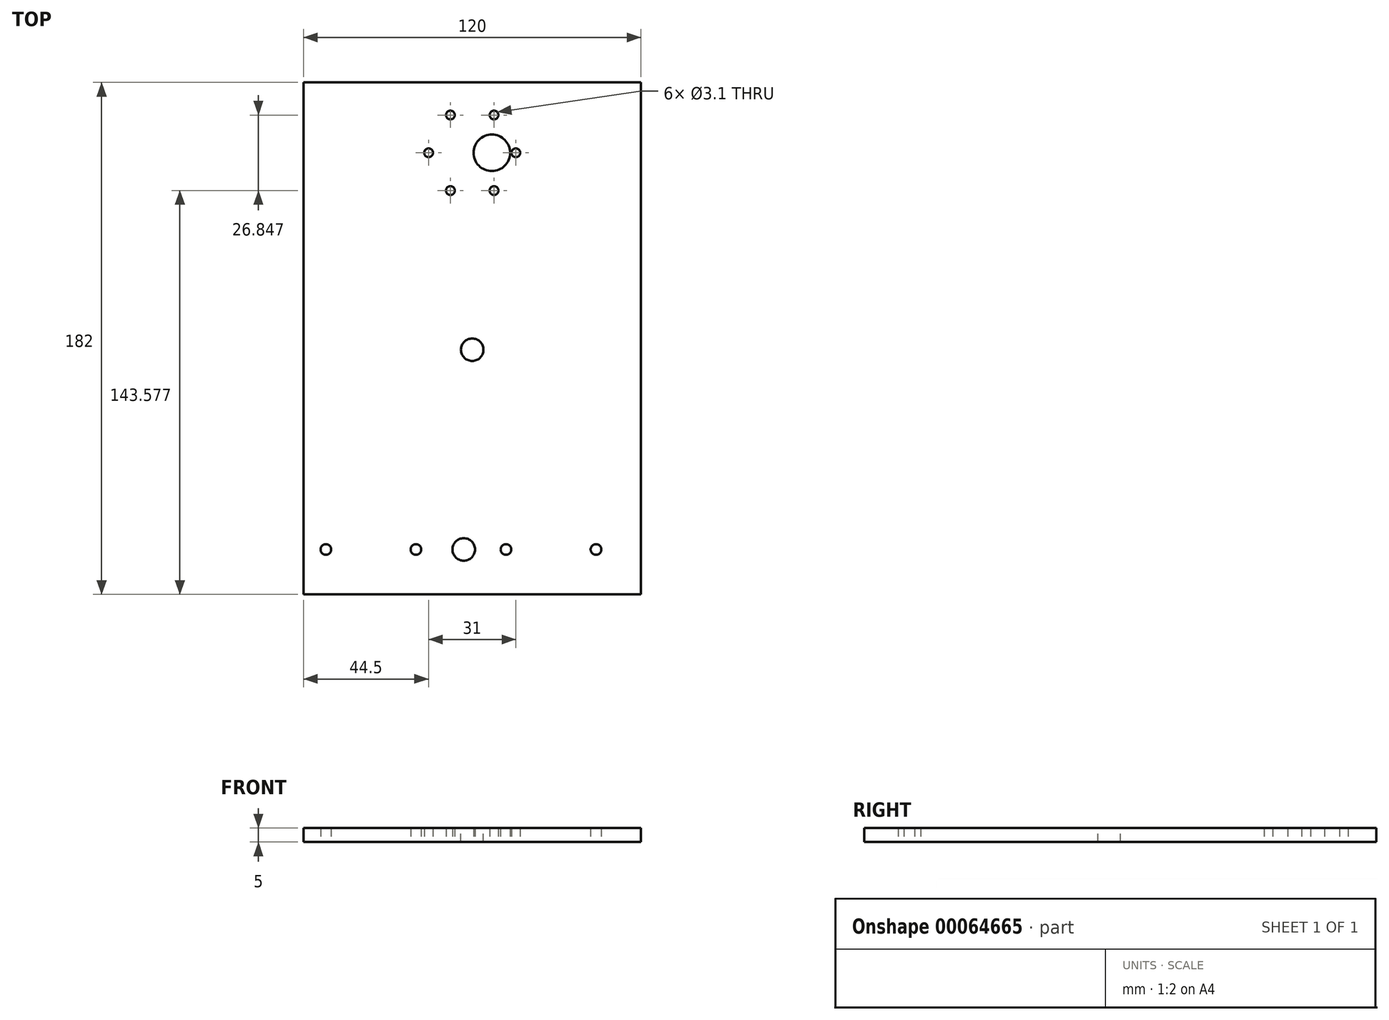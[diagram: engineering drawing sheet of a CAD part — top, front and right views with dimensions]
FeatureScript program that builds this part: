
annotation { "Feature Type Name" : "Feature", "Feature Type Description" : "" }
export const myFeature = defineFeature(function(context is Context, id is Id, definition is map)
    precondition{}
    {
        {
            var Q0;
            Q0=qCreatedBy(makeId("Top.planeOp"),FACE);
            var sketch = newSketch(context, id + "F0", { "sketchPlane" : qUnion([Q0])});
            skLineSegment(sketch, "E0.rect.bottom", {"start": v(-60, -66) * mm, "end": v(60, -66) * mm});
            skLineSegment(sketch, "E0.rect.top", {"start": v(-60, 66) * mm, "end": v(60, 66) * mm});
            skLineSegment(sketch, "E0.rect.left", {"start": v(-60, -66) * mm, "end": v(-60, 66) * mm});
            skLineSegment(sketch, "E0.rect.right", {"start": v(60, -66) * mm, "end": v(60, 66) * mm});
            skPoint(sketch, "E0.rect.middle", {"position": v(0, 0) * mm});
            skLineSegment(sketch, "E1", {"start": v(44, -66) * mm, "end": v(44, -50) * mm, "construction": true});
            skLineSegment(sketch, "E2", {"start": v(60, -66) * mm, "end": v(44, -66) * mm, "construction": true});
            skLineSegment(sketch, "E3", {"start": v(44, -50) * mm, "end": v(60, -50) * mm, "construction": true});
            skCircle(sketch, "E4", {"center": v(44, -50) * mm, "radius": 1.9 * mm});
            skCircle(sketch, "E5.1.0.0", {"center": v(12, -50) * mm, "radius": 1.9 * mm});
            skCircle(sketch, "E5.2.0.0", {"center": v(-20, -50) * mm, "radius": 1.9 * mm});
            skCircle(sketch, "E5.3.0.0", {"center": v(-52, -50) * mm, "radius": 1.9 * mm});
            skLineSegment(sketch, "E5.direction1", {"start": v(44, -50) * mm, "end": v(12, -50) * mm, "construction": true});
            skLineSegment(sketch, "E6", {"start": v(12, -50) * mm, "end": v(-3, -50) * mm, "construction": true});
            skCircle(sketch, "E7", {"center": v(-3, -50) * mm, "radius": 4 * mm});
            skLineSegment(sketch, "E8.top", {"start": v(-60, 116) * mm, "end": v(60, 116) * mm});
            skLineSegment(sketch, "E8.left", {"start": v(-60, 66) * mm, "end": v(-60, 116) * mm});
            skLineSegment(sketch, "E8.right", {"start": v(60, 66) * mm, "end": v(60, 116) * mm});
            skLineSegment(sketch, "E9", {"start": v(0, 116) * mm, "end": v(0, 91) * mm, "construction": true});
            skPoint(sketch, "E9.endSnap0", {"position": v(0, 116) * mm});
            skCircle(sketch, "E10", {"center": v(0, 91) * mm, "radius": 18.5 * mm, "construction": true});
            skLineSegment(sketch, "E11", {"start": v(0, 91) * mm, "end": v(-15.5, 91) * mm, "construction": true});
            skCircle(sketch, "E12", {"center": v(-15.5, 91) * mm, "radius": 1.55 * mm});
            skCircle(sketch, "E13.1.0", {"center": v(-7.75, 77.58) * mm, "radius": 1.55 * mm});
            skCircle(sketch, "E13.2.0", {"center": v(7.75, 77.58) * mm, "radius": 1.55 * mm});
            skCircle(sketch, "E13.3.0", {"center": v(15.5, 91) * mm, "radius": 1.55 * mm});
            skCircle(sketch, "E13.4.0", {"center": v(7.75, 104.42) * mm, "radius": 1.55 * mm});
            skCircle(sketch, "E13.5.0", {"center": v(-7.75, 104.42) * mm, "radius": 1.55 * mm});
            skCircle(sketch, "E14", {"center": v(6.99, 91) * mm, "radius": 6.5 * mm});
            skSolve(sketch);
        }
        {
            var Q0;
            Q0=makeQuery(id+"F0.imprint","IMPRINT",FACE,{"disambiguationData":[TD([[makeQuery(id+"F0.imprint","IMPRINT",EDGE,{"derivedFrom":sQuery(id+"F0.wireOp",EDGE,"E0.rect.bottom")}),1.0]])]});
            var Q1;
            Q1=makeQuery(id+"F0.imprint","IMPRINT",FACE,{"disambiguationData":[TD([[makeQuery(id+"F0.imprint","IMPRINT",EDGE,{"derivedFrom":sQuery(id+"F0.wireOp",EDGE,"E0.rect.top")}),1.0]])]});
            extrude(context, id + "F1", {"entities" : qUnion([Q0, Q1]), "depth" : 5 * mm});
        }
        {
            var Q0;
            Q0=makeQuery(id+"F1.opExtrude","CAP_FACE",FACE,{"disambiguationData":[OSD([sQuery(id+"F0.wireOp",EDGE,"E0.rect.bottom"),sQuery(id+"F0.wireOp",EDGE,"E0.rect.top"),sQuery(id+"F0.wireOp",EDGE,"E0.rect.left"),sQuery(id+"F0.wireOp",EDGE,"E0.rect.right")])],"isStart":false});
            var sketch = newSketch(context, id + "F2", { "sketchPlane" : qUnion([Q0])});
            skLineSegment(sketch, "E15", {"start": v(0, 66) * mm, "end": v(0, 21) * mm, "construction": true});
            skPoint(sketch, "E15.endSnap0", {"position": v(0, 66) * mm});
            skCircle(sketch, "E16", {"center": v(0, 21) * mm, "radius": 4 * mm});
            skSolve(sketch);
        }
        {
            var Q0;
            Q0=makeQuery(id+"F2.imprint","IMPRINT",FACE,{"disambiguationData":[TD([[makeQuery(id+"F2.imprint","IMPRINT",EDGE,{"derivedFrom":sQuery(id+"F2.wireOp",EDGE,"E16")}),1.0]])]});
            var Q1;
            Q1=makeQuery(id+"F2.imprint","IMPRINT",FACE,{"disambiguationData":[TD([[makeQuery(id+"F2.imprint","IMPRINT",EDGE,{"derivedFrom":sQuery(id+"F2.wireOp",EDGE,"1bce6a2f-d512-4ec6-a197-546a77cf71d6")}),1.0]])]});
            extrude(context, id + "F3", {"entities" : qUnion([Q0, Q1]), "operationType" : NewBodyOperationType.REMOVE, "oppositeDirection" : true, "depth" : 25 * mm});
        }
    });
